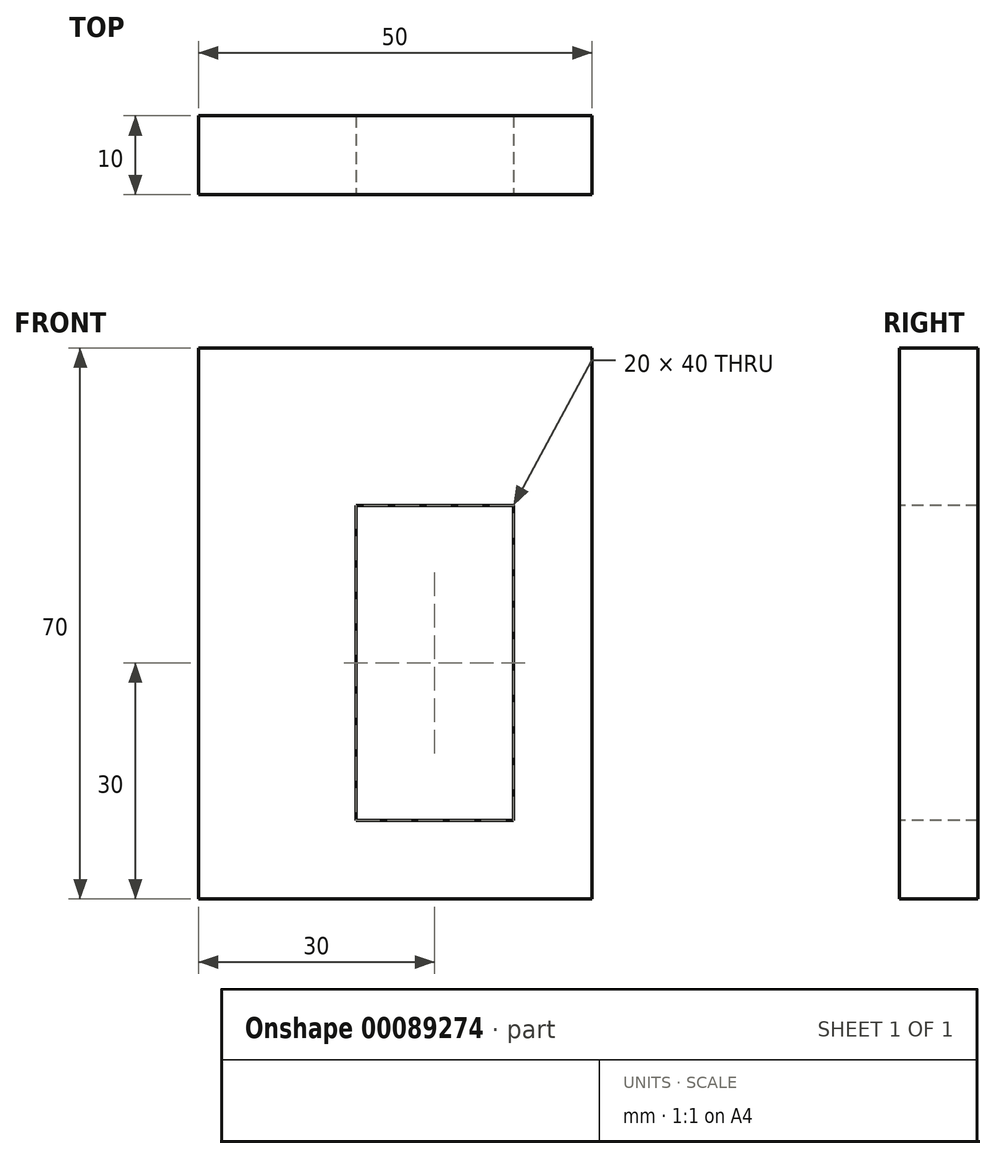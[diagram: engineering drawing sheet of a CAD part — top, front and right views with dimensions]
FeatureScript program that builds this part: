
annotation { "Feature Type Name" : "Feature", "Feature Type Description" : "" }
export const myFeature = defineFeature(function(context is Context, id is Id, definition is map)
    precondition{}
    {
        {
            var Q0;
            Q0=qCreatedBy(makeId("Front.planeOp"),FACE);
            var sketch = newSketch(context, id + "F0", { "sketchPlane" : qUnion([Q0])});
            skLineSegment(sketch, "E0", {"start": v(0, 0) * mm, "end": v(50, 0) * mm});
            skLineSegment(sketch, "E1", {"start": v(50, 0) * mm, "end": v(50, 70) * mm});
            skLineSegment(sketch, "E2", {"start": v(50, 70) * mm, "end": v(0, 70) * mm});
            skLineSegment(sketch, "E3", {"start": v(0, 70) * mm, "end": v(0, 0) * mm});
            skLineSegment(sketch, "E4.bottom", {"start": v(40, 50) * mm, "end": v(20, 50) * mm});
            skLineSegment(sketch, "E4.top", {"start": v(40, 10) * mm, "end": v(20, 10) * mm});
            skLineSegment(sketch, "E4.left", {"start": v(40, 50) * mm, "end": v(40, 10) * mm});
            skLineSegment(sketch, "E4.right", {"start": v(20, 50) * mm, "end": v(20, 10) * mm});
            skSolve(sketch);
        }
        {
            var Q0;
            Q0 = qSketchRegion(id + "F0", true);
            extrude(context, id + "F1", {"entities" : qUnion([Q0]), "oppositeDirection" : true, "depth" : 10 * mm});
        }
    });
